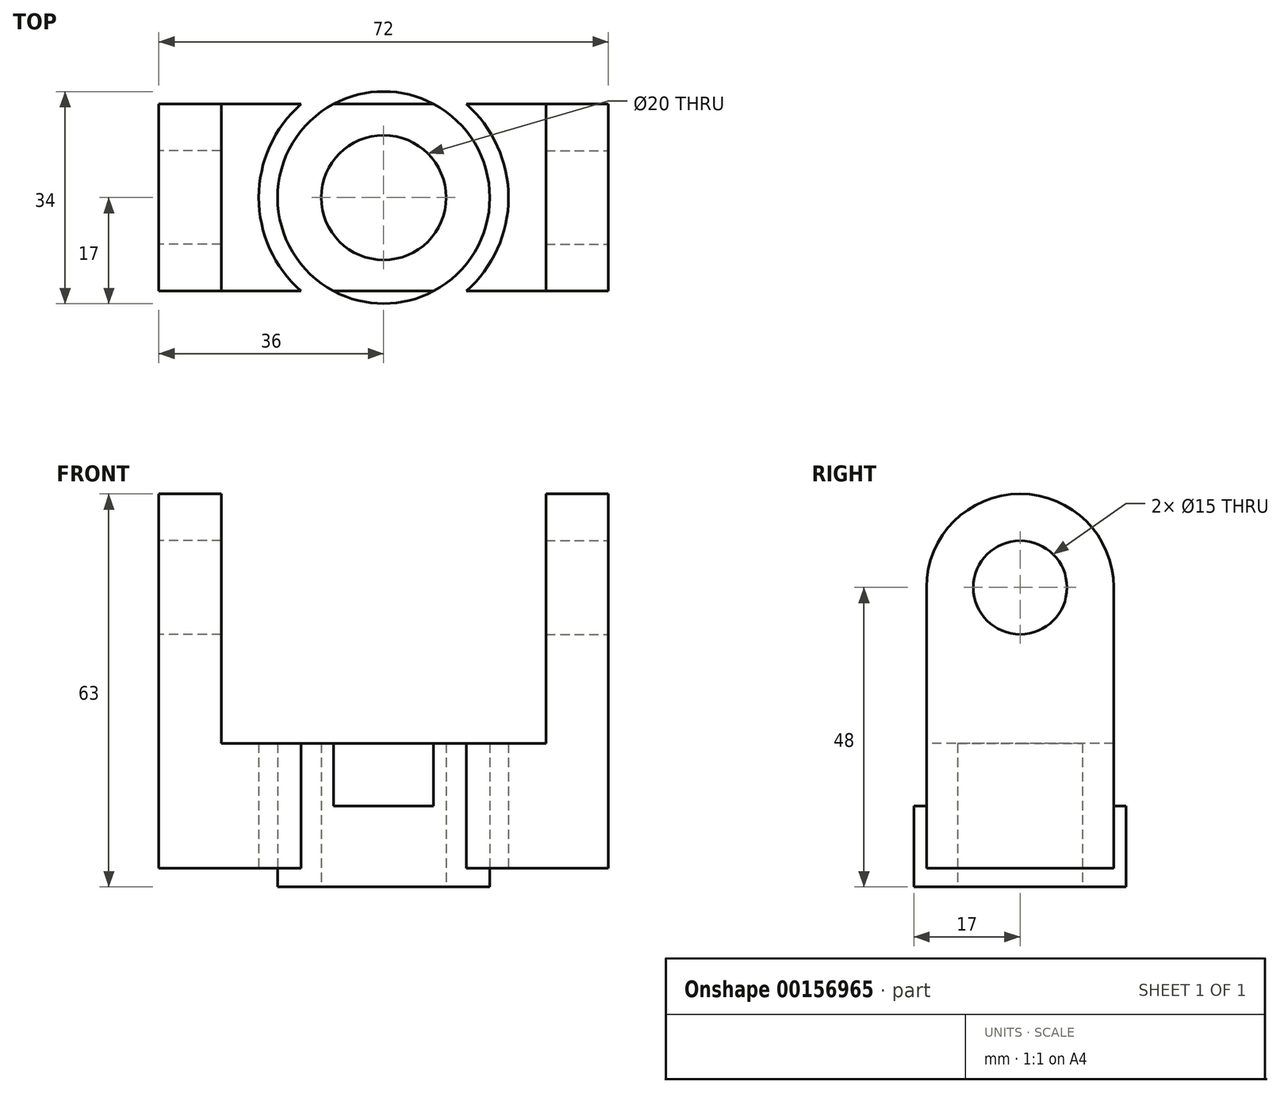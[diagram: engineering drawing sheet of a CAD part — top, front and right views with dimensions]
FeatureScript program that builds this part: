
annotation { "Feature Type Name" : "Feature", "Feature Type Description" : "" }
export const myFeature = defineFeature(function(context is Context, id is Id, definition is map)
    precondition{}
    {
        {
            var Q0;
            Q0=qCreatedBy(makeId("Top.planeOp"),FACE);
            var sketch = newSketch(context, id + "F0", { "sketchPlane" : qUnion([Q0])});
            skCircle(sketch, "E0", {"center": v(0, 0) * mm, "radius": 10 * mm});
            skLineSegment(sketch, "E1.bottom", {"start": v(36, -15) * mm, "end": v(-36, -15) * mm});
            skLineSegment(sketch, "E1.top", {"start": v(36, 15) * mm, "end": v(-36, 15) * mm});
            skLineSegment(sketch, "E1.left", {"start": v(36, -15) * mm, "end": v(36, 15) * mm});
            skLineSegment(sketch, "E1.right", {"start": v(-36, -15) * mm, "end": v(-36, 15) * mm});
            skCircle(sketch, "E2", {"center": v(0, 0) * mm, "radius": 20 * mm});
            skCircle(sketch, "E3", {"center": v(0, 0) * mm, "radius": 17 * mm});
            skSolve(sketch);
        }
        {
            var Q0;
            {var subQ0=sQuery(id+"F0.wireOp",EDGE,"E1.right");Q0=makeQuery(id+"F0.imprint","IMPRINT",FACE,{"disambiguationData":[TD([[makeQuery(id+"F0.imprint","IMPRINT",EDGE,{"derivedFrom":subQ0}),-1.0]])]});}
            var Q1;
            Q1=makeQuery(id+"F0.imprint","IMPRINT",FACE,{"disambiguationData":[TD([[makeQuery(id+"F0.imprint","IMPRINT",EDGE,{"derivedFrom":sQuery(id+"F0.wireOp",EDGE,"E0")}),-1.0]])]});
            var Q2;
            {var subQ0=sQuery(id+"F0.wireOp",EDGE,"E1.left");Q2=makeQuery(id+"F0.imprint","IMPRINT",FACE,{"disambiguationData":[TD([[makeQuery(id+"F0.imprint","IMPRINT",EDGE,{"derivedFrom":subQ0}),1.0]])]});}
            var Q3;
            {var subQ0=sQuery(id+"F0.wireOp",EDGE,"E2");var subQ1=sQuery(id+"F0.wireOp",EDGE,"E1.bottom");var subQ2=makeQuery(id+"F0.imprint","INTERSECT",VERTEX,{"disambiguationData":[OD(1.0)],"derivedFrom":[subQ1,subQ0]});Q3=makeQuery(id+"F0.imprint","IMPRINT",FACE,{"disambiguationData":[TD([[makeQuery(id+"F0.imprint","IMPRINT",EDGE,{"disambiguationData":[TD([[subQ2,1.0]])],"derivedFrom":subQ1}),-1.0]])]});}
            var Q4;
            {var subQ0=sQuery(id+"F0.wireOp",EDGE,"E2");var subQ1=sQuery(id+"F0.wireOp",EDGE,"E1.bottom");var subQ2=makeQuery(id+"F0.imprint","INTERSECT",VERTEX,{"disambiguationData":[OD(0.0)],"derivedFrom":[subQ1,subQ0]});Q4=makeQuery(id+"F0.imprint","IMPRINT",FACE,{"disambiguationData":[TD([[makeQuery(id+"F0.imprint","IMPRINT",EDGE,{"disambiguationData":[TD([[subQ2,-1.0]])],"derivedFrom":subQ1}),-1.0]])]});}
            extrude(context, id + "F1", {"entities" : qUnion([Q0, Q1, Q2, Q3, Q4]), "depth" : 10 * mm});
        }
        {
            var Q0;
            Q0=makeQuery(id+"F0.imprint","IMPRINT",FACE,{"disambiguationData":[TD([[makeQuery(id+"F0.imprint","IMPRINT",EDGE,{"derivedFrom":sQuery(id+"F0.wireOp",EDGE,"E0")}),-1.0]])]});
            var Q1;
            {var subQ0=sQuery(id+"F0.wireOp",EDGE,"E3");var subQ1=sQuery(id+"F0.wireOp",EDGE,"E1.bottom");var subQ2=makeQuery(id+"F0.imprint","INTERSECT",VERTEX,{"disambiguationData":[OD(0.0)],"derivedFrom":[subQ1,subQ0]});Q1=makeQuery(id+"F0.imprint","IMPRINT",FACE,{"disambiguationData":[TD([[makeQuery(id+"F0.imprint","IMPRINT",EDGE,{"disambiguationData":[TD([[subQ2,-1.0]])],"derivedFrom":subQ1}),1.0]])]});}
            var Q2;
            {var subQ0=sQuery(id+"F0.wireOp",EDGE,"E3");var subQ1=sQuery(id+"F0.wireOp",EDGE,"E1.top");var subQ2=makeQuery(id+"F0.imprint","INTERSECT",VERTEX,{"disambiguationData":[OD(0.0)],"derivedFrom":[subQ1,subQ0]});Q2=makeQuery(id+"F0.imprint","IMPRINT",FACE,{"disambiguationData":[TD([[makeQuery(id+"F0.imprint","IMPRINT",EDGE,{"disambiguationData":[TD([[subQ2,-1.0]])],"derivedFrom":subQ1}),-1.0]])]});}
            extrude(context, id + "F2", {"entities" : qUnion([Q0, Q1, Q2]), "operationType" : NewBodyOperationType.ADD, "oppositeDirection" : true, "depth" : 3 * mm});
        }
        {
            var Q0;
            Q0=makeQuery(id+"F1.opExtrude","SWEPT_FACE",FACE,{"disambiguationData":[OSD([sQuery(id+"F0.wireOp",EDGE,"E1.left")])]});
            cPlane(context, id + "F3", {"entities" : qUnion([Q0]), "cplaneType" : CPlaneType.OFFSET, "offset" : 0 * mm, "width" : 150 * mm, "height" : 150 * mm});
        }
        {
            var Q0;
            {var subQ0=sQuery(id+"F0.wireOp",EDGE,"E2");var subQ1=sQuery(id+"F0.wireOp",EDGE,"E1.bottom");var subQ2=makeQuery(id+"F0.imprint","INTERSECT",VERTEX,{"disambiguationData":[OD(0.0)],"derivedFrom":[subQ1,subQ0]});Q0=makeQuery(id+"F0.imprint","IMPRINT",FACE,{"disambiguationData":[TD([[makeQuery(id+"F0.imprint","IMPRINT",EDGE,{"disambiguationData":[TD([[subQ2,-1.0]])],"derivedFrom":subQ1}),1.0]])]});}
            var Q1;
            Q1=makeQuery(id+"F2.opExtrude","CAP_FACE",FACE,{"disambiguationData":[OSD([sQuery(id+"F0.wireOp",EDGE,"E0"),sQuery(id+"F0.wireOp",EDGE,"E3")])],"isStart":false});
            var Q2;
            {var subQ0=sQuery(id+"F0.wireOp",EDGE,"E2");var subQ1=sQuery(id+"F0.wireOp",EDGE,"E1.bottom");var subQ2=makeQuery(id+"F0.imprint","INTERSECT",VERTEX,{"disambiguationData":[OD(0.0)],"derivedFrom":[subQ1,subQ0]});Q2=makeQuery(id+"F0.imprint","IMPRINT",FACE,{"disambiguationData":[TD([[makeQuery(id+"F0.imprint","IMPRINT",EDGE,{"disambiguationData":[TD([[subQ2,-1.0]])],"derivedFrom":subQ1}),-1.0]])]});}
            var Q3;
            {var subQ0=sQuery(id+"F0.wireOp",EDGE,"E2");var subQ1=sQuery(id+"F0.wireOp",EDGE,"E1.top");var subQ2=makeQuery(id+"F0.imprint","INTERSECT",VERTEX,{"disambiguationData":[OD(0.0)],"derivedFrom":[subQ1,subQ0]});Q3=makeQuery(id+"F0.imprint","IMPRINT",FACE,{"disambiguationData":[TD([[makeQuery(id+"F0.imprint","IMPRINT",EDGE,{"disambiguationData":[TD([[subQ2,-1.0]])],"derivedFrom":subQ1}),-1.0]])]});}
            var Q4;
            {var subQ0=sQuery(id+"F0.wireOp",EDGE,"E2");var subQ1=sQuery(id+"F0.wireOp",EDGE,"E1.bottom");var subQ2=makeQuery(id+"F0.imprint","INTERSECT",VERTEX,{"disambiguationData":[OD(1.0)],"derivedFrom":[subQ1,subQ0]});Q4=makeQuery(id+"F0.imprint","IMPRINT",FACE,{"disambiguationData":[TD([[makeQuery(id+"F0.imprint","IMPRINT",EDGE,{"disambiguationData":[TD([[subQ2,1.0]])],"derivedFrom":subQ1}),-1.0]])]});}
            var Q5;
            {var subQ0=sQuery(id+"F0.wireOp",EDGE,"E3");var subQ1=sQuery(id+"F0.wireOp",EDGE,"E1.bottom");var subQ2=makeQuery(id+"F0.imprint","INTERSECT",VERTEX,{"disambiguationData":[OD(0.0)],"derivedFrom":[subQ1,subQ0]});Q5=makeQuery(id+"F0.imprint","IMPRINT",FACE,{"disambiguationData":[TD([[makeQuery(id+"F0.imprint","IMPRINT",EDGE,{"disambiguationData":[TD([[subQ2,-1.0]])],"derivedFrom":subQ1}),1.0]])]});}
            var Q6;
            {var subQ0=sQuery(id+"F0.wireOp",EDGE,"E3");var subQ1=sQuery(id+"F0.wireOp",EDGE,"E1.top");var subQ2=makeQuery(id+"F0.imprint","INTERSECT",VERTEX,{"disambiguationData":[OD(0.0)],"derivedFrom":[subQ1,subQ0]});Q6=makeQuery(id+"F0.imprint","IMPRINT",FACE,{"disambiguationData":[TD([[makeQuery(id+"F0.imprint","IMPRINT",EDGE,{"disambiguationData":[TD([[subQ2,-1.0]])],"derivedFrom":subQ1}),-1.0]])]});}
            extrude(context, id + "F4", {"entities" : qUnion([Q0, Q1, Q2, Q3, Q4, Q5, Q6]), "operationType" : NewBodyOperationType.ADD, "depth" : 10 * mm});
        }
        {
            var Q0;
            Q0=qCreatedBy(id+"F3.planeOp",FACE);
            var sketch = newSketch(context, id + "F5", { "sketchPlane" : qUnion([Q0])});
            skLineSegment(sketch, "E4", {"start": v(-15, 0) * mm, "end": v(15, 0) * mm});
            skLineSegment(sketch, "E5", {"start": v(15, 0) * mm, "end": v(15, 35) * mm});
            skLineSegment(sketch, "E6", {"start": v(-15, 0) * mm, "end": v(-15, 35) * mm});
            skArc(sketch, "E7", {"start": v(15, 35) * mm, "mid": v(0, 50) * mm, "end": v(-15, 35) * mm});
            skCircle(sketch, "E8", {"center": v(0, 35) * mm, "radius": 7.5 * mm});
            skSolve(sketch);
        }
        {
            var Q0;
            Q0=makeQuery(id+"F5.imprint","IMPRINT",FACE,{"disambiguationData":[TD([[makeQuery(id+"F5.imprint","IMPRINT",EDGE,{"derivedFrom":sQuery(id+"F5.wireOp",EDGE,"E4")}),1.0]])]});
            extrude(context, id + "F6", {"entities" : qUnion([Q0]), "operationType" : NewBodyOperationType.ADD, "oppositeDirection" : true, "depth" : 10 * mm});
        }
        {
            var Q0;
            Q0=makeQuery(id+"F1.opExtrude","SWEPT_FACE",FACE,{"disambiguationData":[OSD([sQuery(id+"F0.wireOp",EDGE,"E1.right")])]});
            cPlane(context, id + "F7", {"entities" : qUnion([Q0]), "cplaneType" : CPlaneType.OFFSET, "offset" : 0 * mm, "width" : 150 * mm, "height" : 150 * mm});
        }
        {
            var Q0;
            Q0=qCreatedBy(id+"F7.planeOp",FACE);
            var sketch = newSketch(context, id + "F8", { "sketchPlane" : qUnion([Q0])});
            skLineSegment(sketch, "E9", {"start": v(-15, 0) * mm, "end": v(15, 0) * mm});
            skLineSegment(sketch, "E10", {"start": v(15, 0) * mm, "end": v(15, 35) * mm});
            skLineSegment(sketch, "E11", {"start": v(-15, 0) * mm, "end": v(-15, 35) * mm});
            skArc(sketch, "E12", {"start": v(15, 35) * mm, "mid": v(0, 50) * mm, "end": v(-15, 35) * mm});
            skCircle(sketch, "E13", {"center": v(0, 35) * mm, "radius": 7.5 * mm});
            skSolve(sketch);
        }
        {
            var Q0;
            Q0=makeQuery(id+"F8.imprint","IMPRINT",FACE,{"disambiguationData":[TD([[makeQuery(id+"F8.imprint","IMPRINT",EDGE,{"derivedFrom":sQuery(id+"F8.wireOp",EDGE,"E9")}),1.0]])]});
            extrude(context, id + "F9", {"entities" : qUnion([Q0]), "operationType" : NewBodyOperationType.ADD, "oppositeDirection" : true, "depth" : 10 * mm});
        }
    });
